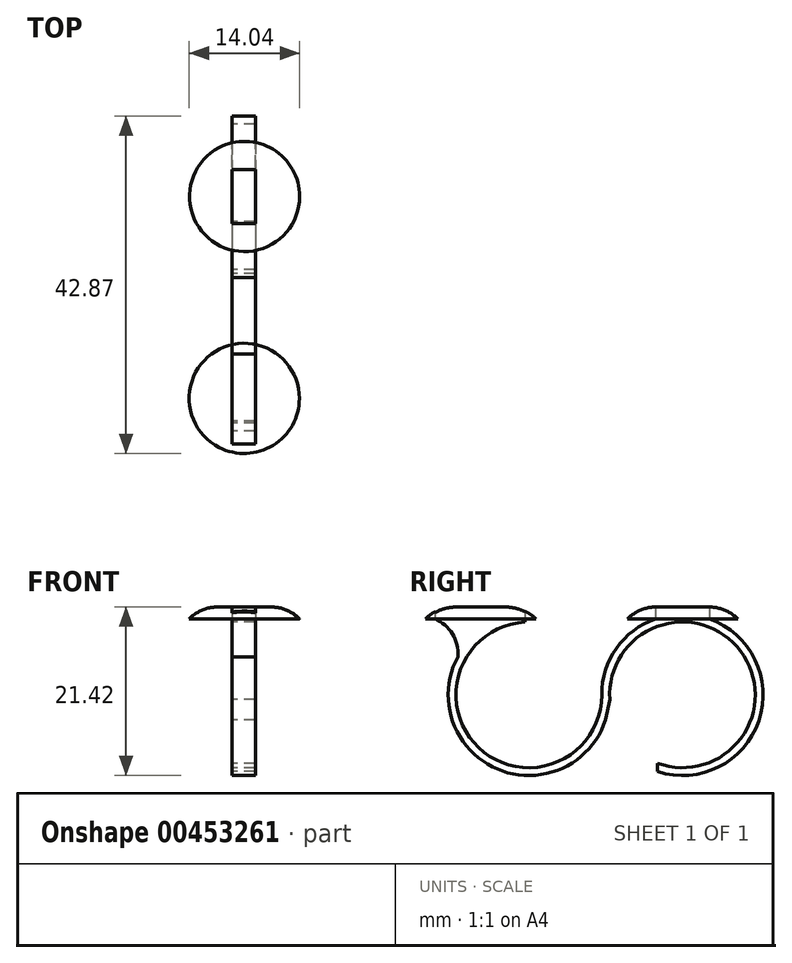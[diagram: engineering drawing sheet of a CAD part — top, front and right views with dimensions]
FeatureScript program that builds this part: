
annotation { "Feature Type Name" : "Feature", "Feature Type Description" : "" }
export const myFeature = defineFeature(function(context is Context, id is Id, definition is map)
    precondition{}
    {
        {
            var Q0;
            Q0=qCreatedBy(makeId("Right.planeOp"),FACE);
            var sketch = newSketch(context, id + "F0", { "sketchPlane" : qUnion([Q0])});
            skArc(sketch, "E0", {"start": v(-3.15, -8.7) * mm, "mid": v(7.4, 5.55) * mm, "end": v(-9.23, -0.6) * mm});
            skArc(sketch, "E1", {"start": v(-3.15, -9.75) * mm, "mid": v(9.7, -3.3) * mm, "end": v(3.44, 9.66) * mm});
            skArc(sketch, "E2", {"start": v(-19.97, 9.24) * mm, "mid": v(-25.87, -6.7) * mm, "end": v(-10.25, 0) * mm});
            skLineSegment(sketch, "E3", {"start": v(-9.75, -3.16) * mm, "end": v(-9.23, -0.6) * mm});
            skLineSegment(sketch, "E4", {"start": v(-3.15, -8.7) * mm, "end": v(-3.15, -9.75) * mm});
            skLineSegment(sketch, "E5", {"start": v(3.44, 9.66) * mm, "end": v(-3.44, 9.66) * mm});
            skArc(sketch, "E6.trimOffspring", {"start": v(-3.44, 9.66) * mm, "mid": v(-8.37, 5.9) * mm, "end": v(-10.25, 0) * mm});
            skLineSegment(sketch, "E7", {"start": v(-19.97, 9.66) * mm, "end": v(-22.94, 9.66) * mm});
            skArc(sketch, "E8.trimOffspring", {"start": v(-28.53, 4.85) * mm, "mid": v(-23.52, -9.43) * mm, "end": v(-9.75, -3.16) * mm});
            skLineSegment(sketch, "E9", {"start": v(-19.97, 9.66) * mm, "end": v(-19.97, 9.24) * mm});
            skPoint(sketch, "E10.orphan", {"position": v(-16.06, 9.66) * mm});
            skArc(sketch, "E11", {"start": v(-28.53, 4.85) * mm, "mid": v(-29.19, 7.74) * mm, "end": v(-31.45, 9.66) * mm});
            skLineSegment(sketch, "E12", {"start": v(-31.45, 9.66) * mm, "end": v(-22.94, 9.66) * mm});
            skSolve(sketch);
        }
        {
            var Q0;
            Q0=makeQuery(id+"F0.imprint","IMPRINT",FACE,{"disambiguationData":[TD([[makeQuery(id+"F0.imprint","IMPRINT",EDGE,{"derivedFrom":sQuery(id+"F0.wireOp",EDGE,"E0")}),-1.0]])]});
            extrude(context, id + "F1", {"entities" : qUnion([Q0]), "depth" : 3 * mm, "offsetDistance" : 25.4 * mm});
        }
        {
            var Q0;
            Q0=makeQuery(id+"F1.opExtrude","SWEPT_FACE",FACE,{"disambiguationData":[OSD([sQuery(id+"F0.wireOp",EDGE,"E7"),sQuery(id+"F0.wireOp",EDGE,"E12")])]});
            var sketch = newSketch(context, id + "F2", { "sketchPlane" : qUnion([Q0])});
            skCircle(sketch, "E13", {"center": v(1.54, -25.62) * mm, "radius": 7 * mm});
            skSolve(sketch);
        }
        {
            var Q0;
            {var subQ0=sQuery(id+"F2.wireOp",EDGE,"E13");var subQ1=makeQuery(id+"F1.opExtrude","CAP_EDGE",EDGE,{"disambiguationData":[OSD([sQuery(id+"F0.wireOp",EDGE,"E7"),sQuery(id+"F0.wireOp",EDGE,"E12")])],"isStart":true});var subQ2=makeQuery(id+"F2.imprint","INTERSECT",VERTEX,{"disambiguationData":[OD(0.0)],"derivedFrom":[subQ1,subQ0]});Q0=makeQuery(id+"F2.imprint","IMPRINT",FACE,{"disambiguationData":[TD([[makeQuery(id+"F2.imprint","IMPRINT",EDGE,{"disambiguationData":[TD([[subQ2,-1.0]])],"derivedFrom":subQ0}),1.0]])]});}
            var Q1;
            {var subQ0=sQuery(id+"F2.wireOp",EDGE,"E13");var subQ1=sQuery(id+"F0.wireOp",EDGE,"E12");var subQ4=sQuery(id+"F0.wireOp",EDGE,"E7");var subQ10=makeQuery(id+"F1.opExtrude","CAP_EDGE",EDGE,{"disambiguationData":[OSD([subQ4,subQ1])],"isStart":true});var subQ13=makeQuery(id+"F2.imprint","INTERSECT",VERTEX,{"disambiguationData":[OD(0.0)],"derivedFrom":[subQ10,subQ0]});Q1=makeQuery(id+"F2.imprint","IMPRINT",FACE,{"disambiguationData":[TD([[makeQuery(id+"F2.imprint","IMPRINT",EDGE,{"disambiguationData":[TD([[subQ13,1.0]])],"derivedFrom":subQ0}),1.0]])]});}
            var Q2;
            {var subQ0=sQuery(id+"F2.wireOp",EDGE,"E13");var subQ1=sQuery(id+"F0.wireOp",EDGE,"E7");var subQ2=makeQuery(id+"F1.opExtrude","SWEPT_EDGE",EDGE,{"disambiguationData":[OSD([subQ1,sQuery(id+"F0.wireOp",EDGE,"E9")])]});var subQ3=makeQuery(id+"F2.imprint","INTERSECT",VERTEX,{"derivedFrom":[subQ2,subQ0]});Q2=makeQuery(id+"F2.imprint","IMPRINT",FACE,{"disambiguationData":[TD([[makeQuery(id+"F2.imprint","IMPRINT",EDGE,{"disambiguationData":[TD([[subQ3,1.0]])],"derivedFrom":subQ0}),1.0]])]});}
            extrude(context, id + "F3", {"entities" : qUnion([Q0, Q1, Q2]), "operationType" : NewBodyOperationType.ADD, "depth" : 1.5 * mm, "offsetDistance" : 25.4 * mm});
        }
        {
            var Q0;
            Q0=makeQuery(id+"F3.opExtrude","CAP_EDGE",EDGE,{"disambiguationData":[OSD([sQuery(id+"F2.wireOp",EDGE,"E13")])],"isStart":false});
            fillet(context, id + "F4", {"entities" : qUnion([Q0]), "radius" : 5.08 * mm, "tangentPropagation" : true, "allowEdgeOverflow" : false});
        }
        {
            var Q0;
            Q0=makeQuery(id+"F1.opExtrude","SWEPT_FACE",FACE,{"disambiguationData":[OSD([sQuery(id+"F0.wireOp",EDGE,"E5")])]});
            var sketch = newSketch(context, id + "F5", { "sketchPlane" : qUnion([Q0])});
            skCircle(sketch, "E14", {"center": v(1.58, 0.03) * mm, "radius": 7 * mm});
            skSolve(sketch);
        }
        {
            var Q0;
            Q0=makeQuery(id+"F5.imprint","IMPRINT",FACE,{"disambiguationData":[TD([[makeQuery(id+"F5.imprint","IMPRINT",EDGE,{"derivedFrom":sQuery(id+"F5.wireOp",EDGE,"E14")}),1.0]])]});
            extrude(context, id + "F6", {"entities" : qUnion([Q0]), "depth" : 1.5 * mm, "offsetDistance" : 25.4 * mm});
        }
        {
            var Q0;
            Q0=makeQuery(id+"F6.opExtrude","CAP_EDGE",EDGE,{"disambiguationData":[OSD([sQuery(id+"F5.wireOp",EDGE,"E14")])],"isStart":false});
            fillet(context, id + "F7", {"entities" : qUnion([Q0]), "radius" : 5.08 * mm, "tangentPropagation" : true, "allowEdgeOverflow" : false});
        }
    });
